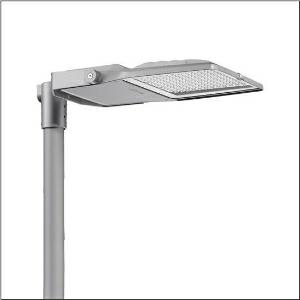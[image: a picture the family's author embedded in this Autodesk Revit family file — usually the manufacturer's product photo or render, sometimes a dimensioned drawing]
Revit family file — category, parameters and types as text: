
# Revit family: floodlight_fl_21_iq_midi___pl61_5xa7782e2c3a_85c4
name_source: partatom
category: Lighting Fixtures
units: mm (PartAtom-declared; Revit-internal decimal feet)

## family parameters
Cut with Voids When Loaded = No
Host = Face
Light Source = No
Part Type = Normal
Room Calculation Point = No
Round Connector Dimension = Use Diameter
Shared = No

## types (1)
- --- (1 x LED, 26360 lm, 208.1 W, 3000K)
    Apparent Load = 208 VA
    CIE Flux Codes = 33 65 98 100 100
    Color Rendering = 70
    Color Temperature = 3000K
    Default Elevation = 1800 mm
    Description = Floodlight FL 21 iQ midi, floodlight, primary light control with lens, of PMMA, primary optical cover: protective disc, of toughened safety glass, transparent, light distribution: PL61, light emission: direct distribution, installation type: surface-mounted, lamps: LED, High Power LED, rated values: 26.360lm | 208,1W | 126,7lm/W (begin service life); end service life: 26.360lm | 227,1W; at 50% lumin. flux: 13.180lm | 90,1W | 146,3lm/W, colour temperature: 3000K, colour rendering: CRI > 70, light colour: 730, light setting 1 begin service life: 100% | 26.360lm | 208,1W | 126,7lm/W | 3.000K, light setting 1 end service life: 227,1W, further light settings possible, control: optimised constant luminous flux control (CLO 2.0), Desk-Remote (wireless, voltage-free reading and setting of iQ features in the workshop via application-optimized NFC function/RFID function), Smart-Wire, Night-Set, Temp-Guard, Auto-Match, Street-Remote, pre-setting: linear dimming characteristic, with terminal, 6-pole, mains connection: 220..240V, AC, 50/60Hz, luminaire housing, of diecast aluminium, powder-coated, SITECO metallic grey (DB 702S), corrosivity category C5 mid according to DIN EN ISO 12944suitable for swimming poolschlorine-resistant, sealing non-destructively replaceable, please order mast flange separately, mast bracket, of steel, galvanised, powder-coated, SITECO metallic grey (DB 702S), protection rating (complete): IP66, insulation class (complete): insulation class II (safety insulation), certification: CE, ENEC, VDE, protection symbol: D, impact resistance: IK08, permissible operating ambient temperature: -40..+40°C, permissible operating ambient temperature for outdoor applications: -40..+50°C, standard: DIN EN 12944, LABS conformity tested according to VDMA 24364:2018-05, packaging unit: 1 piece

Light Distribution: PL61
    Height = 76 mm
    Lamp = 1 x LED
    Lamp Light Flux = 26360 lm
    Lamp Power = 208.1 W
    Lamp count = 1
    Length = 657 mm
    Luminous efficacy = 127 lm/W
    Manufacturer = Siteco
    ModVariant = No
    Model = 5XA7782E2C3A
    Number of Poles = 1
    OnlyDefault = Yes
    Power Factor = 1
    Product Name = Floodlight FL 21 iQ midi | PL61
    Product group = floodlight | pylon annexe
    ProductGroupID = 6201
    Protection Class = Protection class II
    Protection Degree = IP 66
    RLX_Detail_Level = 1
    RLX_Emergency_Light_Flux = 0 lm
    RLX_Emergency_Type = 0
    RLX_Emergency_Type_DB = No
    RlxData = <blob elided: 154033 chars, md5=015e523f>
    Socket = socket
    Standby Power = 0 W
    System Light Flux = 26360 lm
    System Power = 208 W
    Type Comments = factory setting: luminous flux: 100 % | dim-lin: 254 | 710 mA
    Type Image = l_1007123.jpg
    URL = http://relux.com
    VarID = @adj_108693
    Voltage = 0 V
    Weight = 0.00 kg
    Width = 442 mm

## geometry (parser evidence)
native form markers: Blend x4, Sweep x12
no freeform markers — native parametric forms only
